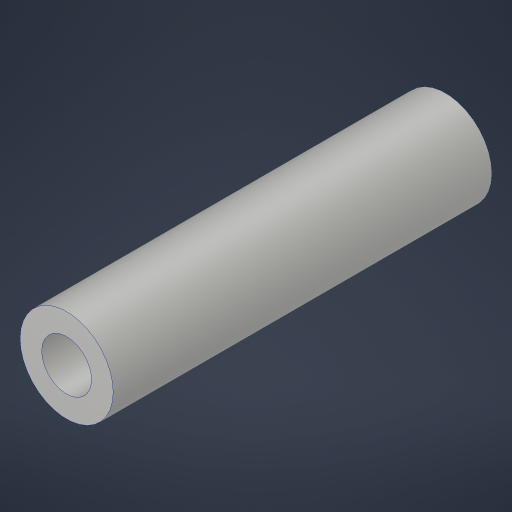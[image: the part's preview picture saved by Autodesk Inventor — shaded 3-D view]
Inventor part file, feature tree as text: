
AUTODESK INVENTOR PART (.ipt)
format: ipt  version: 2023.4 (Build 274418000, 418)  size: 174,080 bytes
history: native  units: in
note: dims shown in document units (in); Inventor stores cm internally (conversion verified against a paired STEP export)
features: extrude x1, hole x1
ambient origin geometry x8: Origin, YZ Plane, XZ Plane, XY Plane, X Axis, Y Axis, Z Axis, Center Point
bodies: Solid1 (feature_tree)
feature tree (2):
  extrude  "Extrusion1"  Depth=1.5249in
  hole  "Hole1"  [1 undecoded]
note: 1 required parameter value undecoded (feature->parameter linkage not recoverable at this tier; creation-order binding heuristic only, values carry confidence <= 0.55)
